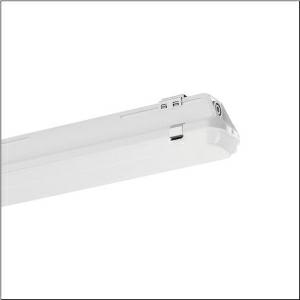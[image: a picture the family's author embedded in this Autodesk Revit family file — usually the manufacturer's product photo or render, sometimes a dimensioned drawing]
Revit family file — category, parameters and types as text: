
# Revit family: monsun_11_51fp20mp480h
name_source: partatom
category: Lighting Fixtures
units: mm (PartAtom-declared; Revit-internal decimal feet)

## family parameters
Cut with Voids When Loaded = No
Host = Face
Light Source = No
Part Type = Normal
Room Calculation Point = No
Round Connector Dimension = Use Diameter
Shared = No

## types (1)
- --- (1 x LED, 8220 lm, 52.3 W, 4000K)
    Apparent Load = 52 VA
    CIE Flux Codes = 45 75 93 94 100
    Color Rendering = 80
    Color Temperature = 4000K
    Default Elevation = 1800 mm
    Description = Monsun 11, damp-proof luminaire, chain hanger, primary optical cover: enclosure, of PC, light emission: direct distribution, primary light characteristic: symmetric, installation type: suspended mounting, surface-mounted, horizontal mounting, vertical mounting, LED, rated luminous flux: 8.220lm, luminous efficacy: 157lm/W, light colour: 840, colour temperature: 4000K, control gear: ON/OFF Multilumen, with terminal, 3-pole, max. 2.5mm², mains connection: 220..240V, AC, 50/60Hz, rated input power: 52W, luminaire housing, of glass-fibre reinforced polyester, uncoated, bright grey, incl. chain hanger, length: 1.590mm, width: 90mm, height: 88mm, clip for enclosure, of stainless steel (V2A), ceiling mounting element, of stainless steel (V2A), chain hanger, of stainless steel (V2A), protection rating (complete): IP66, insulation class (complete): insulation class I (protective earthing), certification: CE, ENEC, VDE, UKCA, protection symbol: D, impact resistance: IK08, permissible operating ambient temperature: -35..+40°C, standard: EN 50419, EN 60598-2-1, no direct snow, no direct sun, no direct rain, for indoor or canopied outdoor use, corresponds to IFS (International Featured Standards) requirements for safety and quality in the food industry, contact your sales advisor before using the luminaires in applications with unclear chemical exposure, large temperature fluctuations or condensation-forming humidity, LABS conformity tested according to VDMA 24364:2018-05, packaging unit: 1 piece
    Height = 89 mm
    Lamp = 1 x LED
    Lamp Light Flux = 8220 lm
    Lamp Power = 52.3 W
    Lamp count = 1
    Length = 1590 mm
    Luminous efficacy = 157 lm/W
    Manufacturer = Siteco
    ModVariant = No
    Model = 51FP20MP480H
    Mounting Place = Ceiling
    Mounting Type = Surface mounted
    Number of Poles = 1
    OnlyDefault = Yes
    Power Factor = 1
    Product Name = Monsun 11
    Product group = damp-proof luminaire
    ProductGroupID = 300
    Protection Class = Protection class I
    Protection Degree = IP 66
    RLX_Detail_Level = 1
    RLX_Emergency_Light_Flux = 0 lm
    RLX_Emergency_Type = 0
    RLX_Emergency_Type_DB = No
    RlxData = <blob elided: 89749 chars, md5=bf395f70>
    Socket = socket
    Standby Power = 0 W
    System Light Flux = 8220 lm
    System Power = 52 W
    Type Comments = factory setting: luminous flux: 100 % | (A | C | E) | 120 mA
    Type Image = l_1349237.jpg
    URL = http://relux.com
    VarID = @adj_195879
    Voltage = 0 V
    Weight = 0.00 kg
    Width = 90 mm

## geometry (parser evidence)
native form markers: Blend x4, Sweep x13
no freeform markers — native parametric forms only
